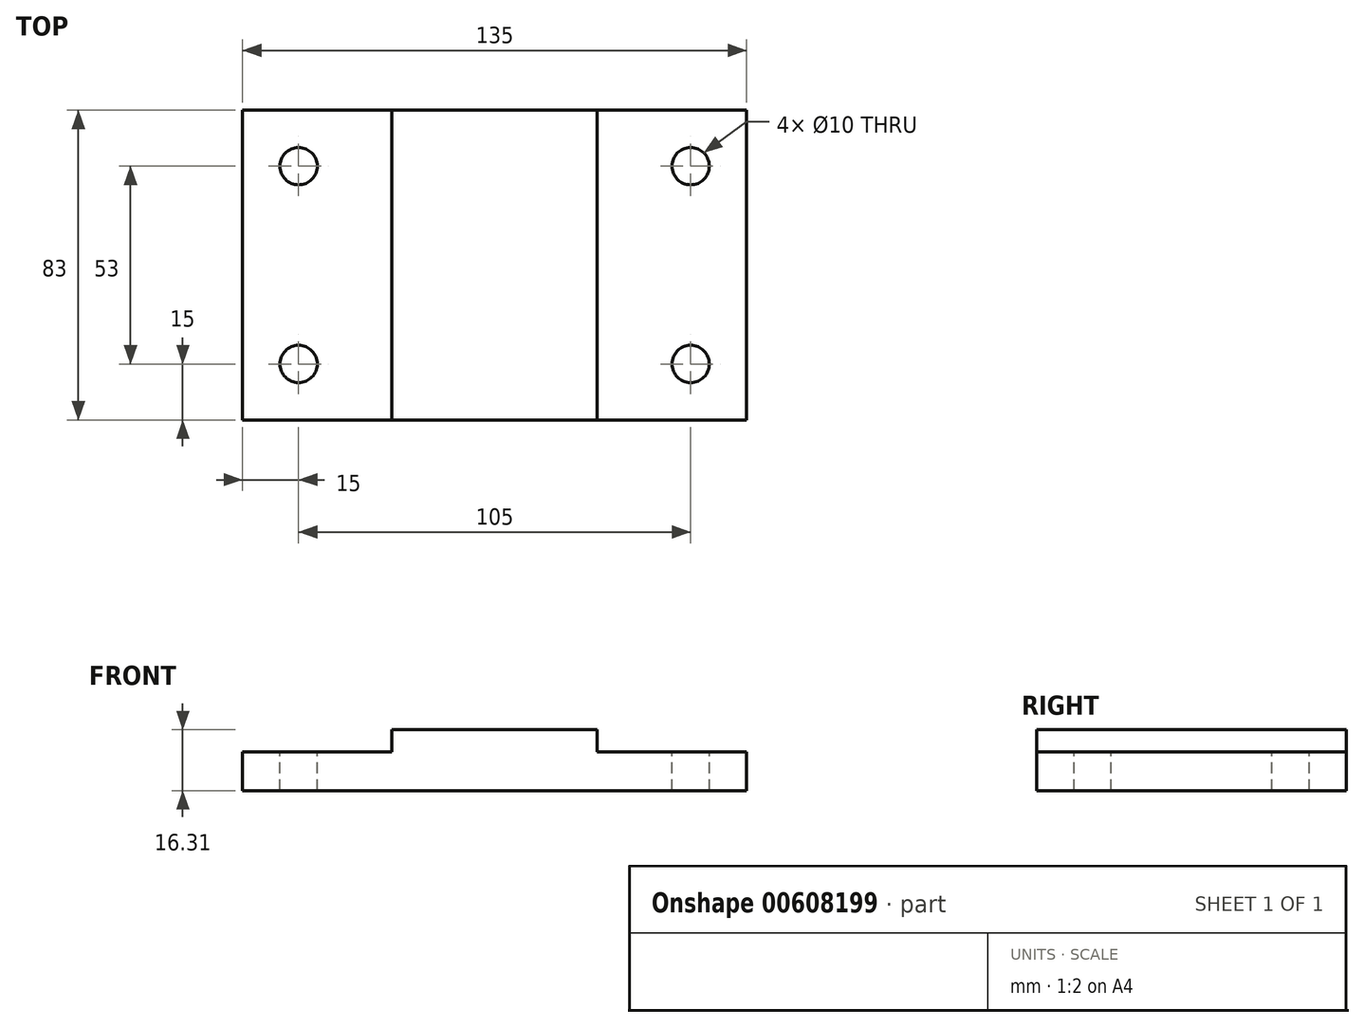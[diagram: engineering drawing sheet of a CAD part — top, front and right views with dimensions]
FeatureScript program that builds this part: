
annotation { "Feature Type Name" : "Feature", "Feature Type Description" : "" }
export const myFeature = defineFeature(function(context is Context, id is Id, definition is map)
    precondition{}
    {
        {
            var Q0;
            Q0=qCreatedBy(makeId("Top.planeOp"),FACE);
            var sketch = newSketch(context, id + "F0", { "sketchPlane" : qUnion([Q0])});
            skLineSegment(sketch, "E0.bottom", {"start": v(-67.5, 41.5) * mm, "end": v(67.5, 41.5) * mm});
            skLineSegment(sketch, "E0.top", {"start": v(-67.5, -41.5) * mm, "end": v(67.5, -41.5) * mm});
            skLineSegment(sketch, "E0.left", {"start": v(-67.5, 41.5) * mm, "end": v(-67.5, -41.5) * mm});
            skLineSegment(sketch, "E0.right", {"start": v(67.5, 41.5) * mm, "end": v(67.5, -41.5) * mm});
            skPoint(sketch, "E0.middle", {"position": v(0, 0) * mm});
            skLineSegment(sketch, "E1.0", {"start": v(-27.5, 41.5) * mm, "end": v(-27.5, -41.5) * mm});
            skLineSegment(sketch, "E2.0", {"start": v(27.5, 41.5) * mm, "end": v(27.5, -41.5) * mm});
            skSolve(sketch);
        }
        {
            var Q0;
            Q0 = qSketchRegion(id + "F0", true);
            extrude(context, id + "F1", {"entities" : qUnion([Q0]), "oppositeDirection" : true, "depth" : 10.3 * mm, "offsetDistance" : 25 * mm});
        }
        {
            var Q0;
            Q0=makeQuery(id+"F1.opExtrude","CAP_FACE",FACE,{"disambiguationData":[OSD([sQuery(id+"F0.wireOp",EDGE,"E0.bottom"),sQuery(id+"F0.wireOp",EDGE,"E0.top"),sQuery(id+"F0.wireOp",EDGE,"E0.left"),sQuery(id+"F0.wireOp",EDGE,"E0.right")])],"isStart":true});
            var sketch = newSketch(context, id + "F2", { "sketchPlane" : qUnion([Q0])});
            skCircle(sketch, "E3", {"center": v(52.5, 26.5) * mm, "radius": 5 * mm});
            skCircle(sketch, "E4", {"center": v(52.5, -26.5) * mm, "radius": 5 * mm});
            skLineSegment(sketch, "E5", {"start": v(0, 41.5) * mm, "end": v(0, -41.5) * mm});
            skCircle(sketch, "E6.MirrorC", {"center": v(-52.5, 26.5) * mm, "radius": 5 * mm});
            skCircle(sketch, "E7.MirrorC", {"center": v(-52.5, -26.5) * mm, "radius": 5 * mm});
            skSolve(sketch);
        }
        {
            var Q0;
            Q0 = qSketchRegion(id + "F2", true);
            extrude(context, id + "F3", {"entities" : qUnion([Q0]), "operationType" : NewBodyOperationType.REMOVE, "endBound" : BoundingType.THROUGH_ALL, "oppositeDirection" : true, "depth" : 25 * mm, "offsetDistance" : 25 * mm});
        }
        {
            var Q0;
            {var subQ0=sQuery(id+"F0.wireOp",EDGE,"E1.0");Q0=makeQuery(id+"F0.imprint","IMPRINT",FACE,{"disambiguationData":[TD([[makeQuery(id+"F0.imprint","IMPRINT",EDGE,{"derivedFrom":subQ0}),1.0]])]});}
            extrude(context, id + "F4", {"entities" : qUnion([Q0]), "operationType" : NewBodyOperationType.ADD, "depth" : 6 * mm, "offsetDistance" : 25 * mm});
        }
        {
            var Q0;
            Q0=qCreatedBy(makeId("Front.planeOp"),FACE);
            cPlane(context, id + "F5", {"entities" : qUnion([Q0]), "cplaneType" : CPlaneType.OFFSET, "offset" : 26.5 * mm, "width" : 150 * mm, "height" : 150 * mm});
        }
    });
